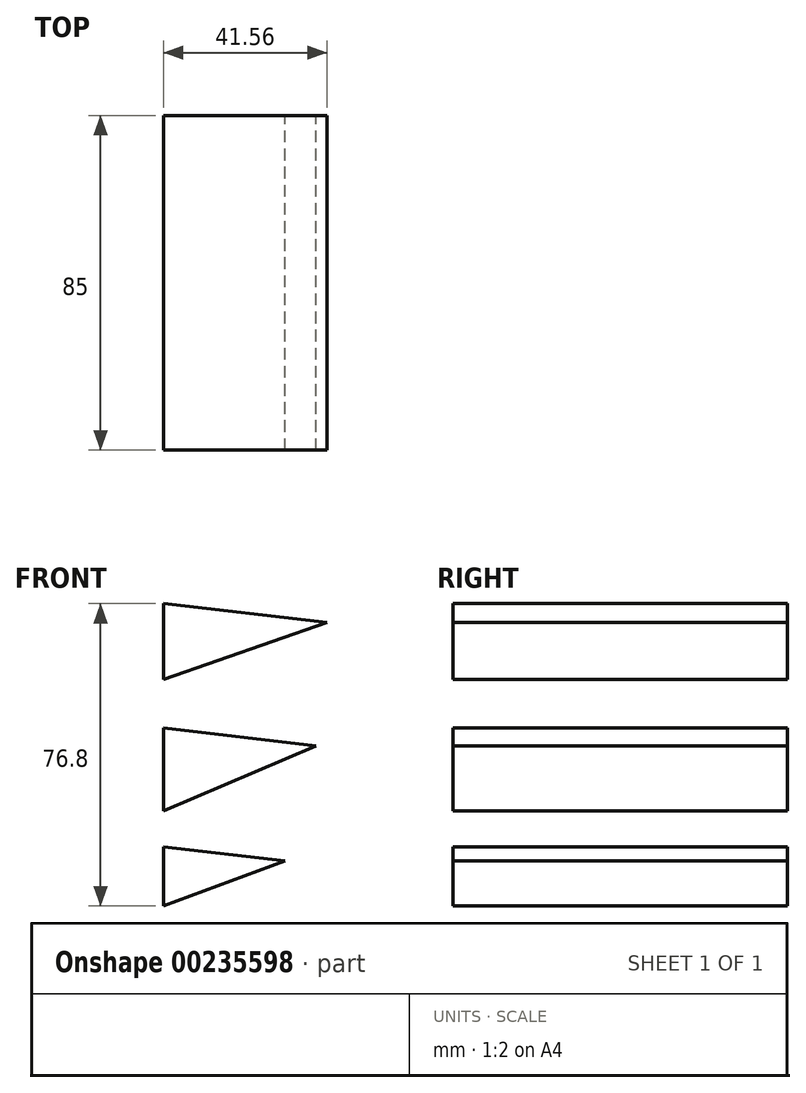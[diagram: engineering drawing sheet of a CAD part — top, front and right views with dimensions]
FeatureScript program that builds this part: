
annotation { "Feature Type Name" : "Feature", "Feature Type Description" : "" }
export const myFeature = defineFeature(function(context is Context, id is Id, definition is map)
    precondition{}
    {
        {
            var Q0;
            Q0=qCreatedBy(makeId("Front.planeOp"),FACE);
            var sketch = newSketch(context, id + "F0", { "sketchPlane" : qUnion([Q0])});
            skLineSegment(sketch, "E0", {"start": v(-30.91, -47.11) * mm, "end": v(-30.91, 38.12) * mm});
            skLineSegment(sketch, "E1", {"start": v(-30.91, 38.12) * mm, "end": v(10.65, 33.3) * mm});
            skLineSegment(sketch, "E2", {"start": v(-30.91, 18.84) * mm, "end": v(10.65, 33.3) * mm});
            skLineSegment(sketch, "E3", {"start": v(-30.91, 6.5) * mm, "end": v(7.85, 2) * mm});
            skLineSegment(sketch, "E4", {"start": v(-30.91, -14.59) * mm, "end": v(7.85, 2) * mm});
            skLineSegment(sketch, "E5", {"start": v(-30.91, -23.62) * mm, "end": v(0, -27.2) * mm});
            skLineSegment(sketch, "E6", {"start": v(-30.91, -38.68) * mm, "end": v(0, -27.2) * mm});
            skSolve(sketch);
        }
        {
            var Q0;
            Q0 = qSketchRegion(id + "F0", true);
            extrude(context, id + "F1", {"entities" : qUnion([Q0]), "depth" : 85 * mm});
        }
    });
